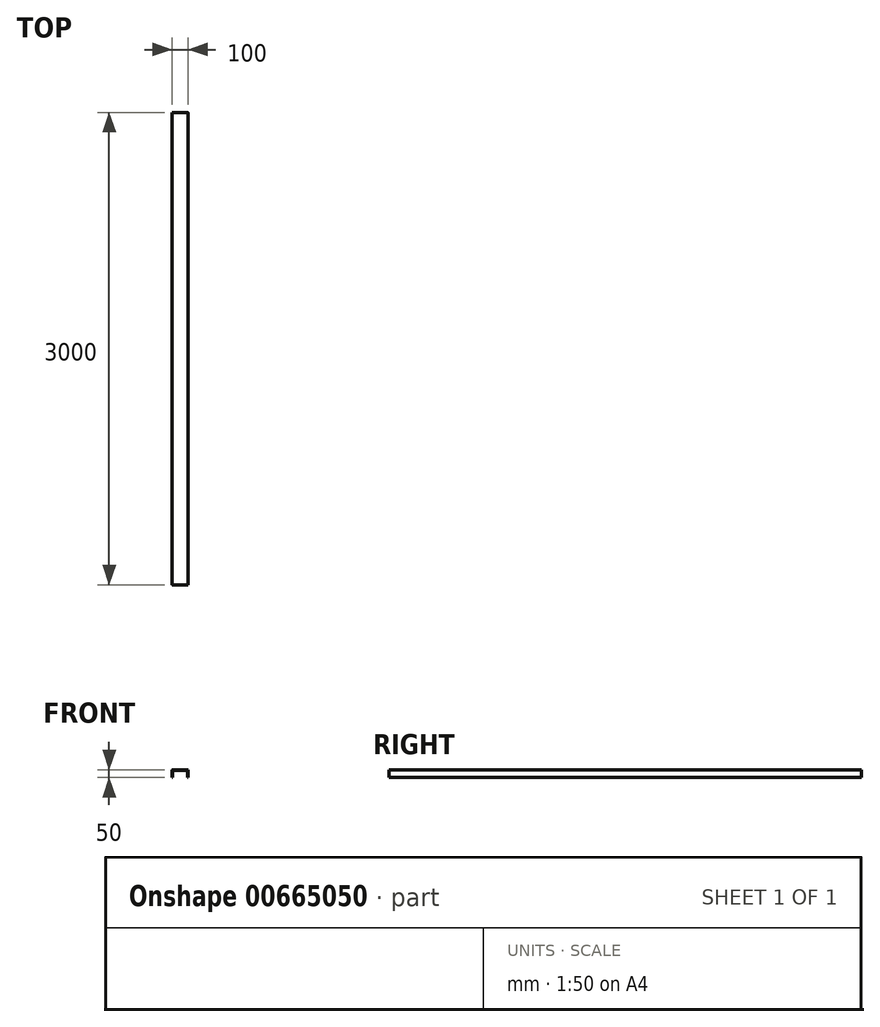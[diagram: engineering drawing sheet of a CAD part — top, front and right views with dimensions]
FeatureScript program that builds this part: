
annotation { "Feature Type Name" : "Feature", "Feature Type Description" : "" }
export const myFeature = defineFeature(function(context is Context, id is Id, definition is map)
    precondition{}
    {
        {
            var Q0;
            Q0=qCreatedBy(makeId("Front.planeOp"),FACE);
            var sketch = newSketch(context, id + "F0", { "sketchPlane" : qUnion([Q0])});
            skLineSegment(sketch, "E0.bottom", {"start": v(-47, 25) * mm, "end": v(47, 25) * mm});
            skLineSegment(sketch, "E0.left", {"start": v(-50, 22) * mm, "end": v(-50, -25) * mm});
            skLineSegment(sketch, "E0.right", {"start": v(50, 22) * mm, "end": v(50, -25) * mm});
            skPoint(sketch, "E0.middle", {"position": v(0, 0) * mm});
            skPoint(sketch, "E1.visualSharp", {"position": v(-50, 25) * mm});
            skArc(sketch, "E1.filletArc", {"start": v(-47, 25) * mm, "mid": v(-49.12, 24.12) * mm, "end": v(-50, 22) * mm});
            skPoint(sketch, "E2.visualSharp", {"position": v(50, 25) * mm});
            skArc(sketch, "E2.filletArc", {"start": v(50, 22) * mm, "mid": v(49.12, 24.12) * mm, "end": v(47, 25) * mm});
            skLineSegment(sketch, "E3.0", {"start": v(-47, 19) * mm, "end": v(-47, -25) * mm});
            skLineSegment(sketch, "E3.1", {"start": v(-44, 22) * mm, "end": v(44, 22) * mm});
            skLineSegment(sketch, "E3.2", {"start": v(47, 19) * mm, "end": v(47, -25) * mm});
            skLineSegment(sketch, "E4", {"start": v(-50, -25) * mm, "end": v(-47, -25) * mm});
            skLineSegment(sketch, "E5", {"start": v(50, -25) * mm, "end": v(47, -25) * mm});
            skArc(sketch, "E6.filletArc", {"start": v(-44, 22) * mm, "mid": v(-46.12, 21.12) * mm, "end": v(-47, 19) * mm});
            skArc(sketch, "E7.filletArc", {"start": v(47, 19) * mm, "mid": v(46.12, 21.12) * mm, "end": v(44, 22) * mm});
            skSolve(sketch);
        }
        {
            var Q0;
            Q0=makeQuery(id+"F0.imprint","IMPRINT",FACE,{"disambiguationData":[TD([[makeQuery(id+"F0.imprint","IMPRINT",EDGE,{"derivedFrom":sQuery(id+"F0.wireOp",EDGE,"E0.bottom")}),-1.0]])]});
            extrude(context, id + "F1", {"entities" : qUnion([Q0]), "endBound" : BoundingType.SYMMETRIC, "depth" : 3000 * mm, "offsetDistance" : 25 * mm});
        }
    });
